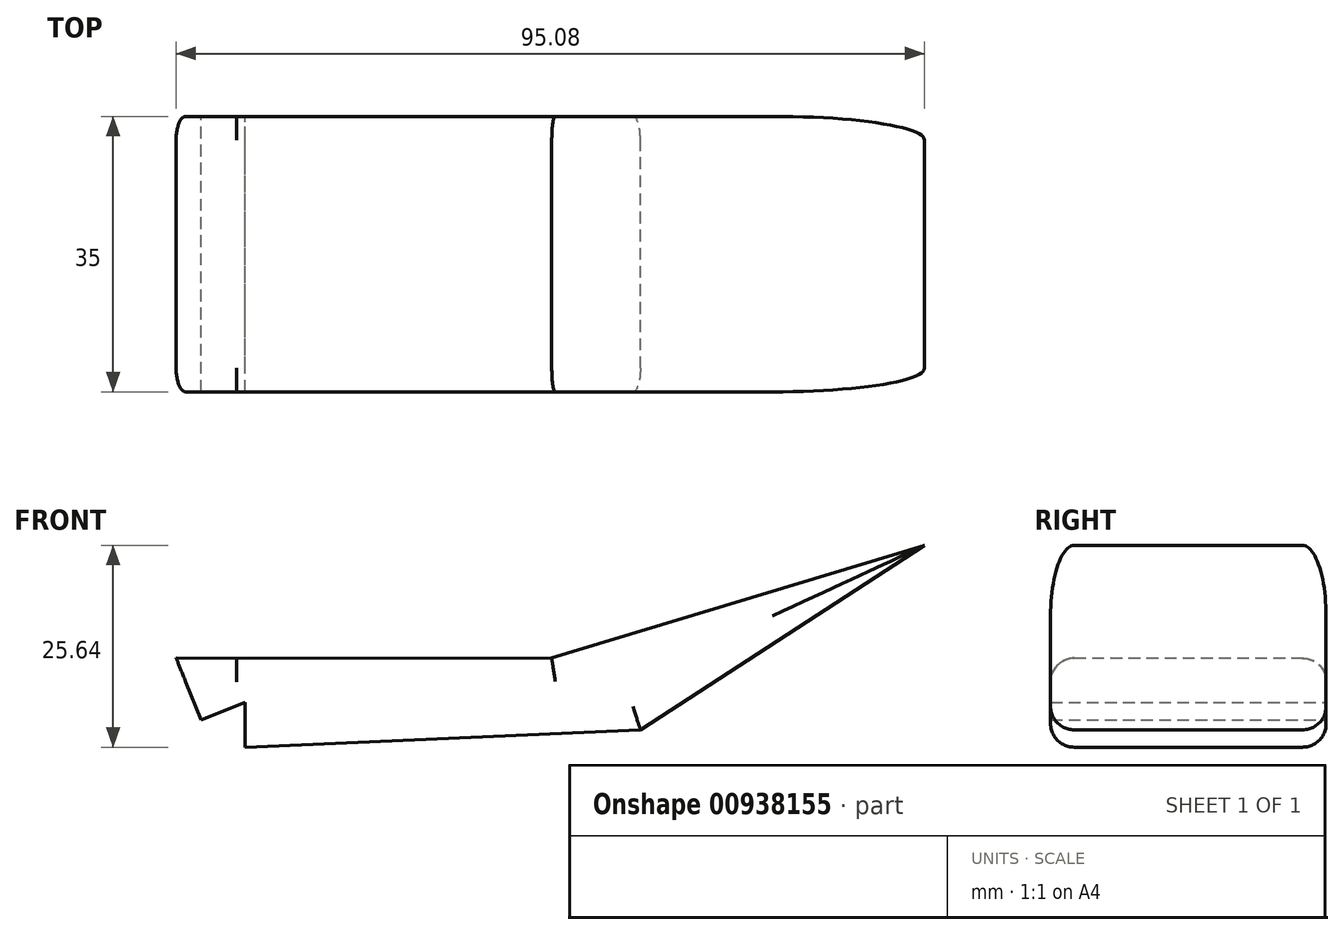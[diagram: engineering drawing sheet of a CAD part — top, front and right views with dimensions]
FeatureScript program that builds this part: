
annotation { "Feature Type Name" : "Feature", "Feature Type Description" : "" }
export const myFeature = defineFeature(function(context is Context, id is Id, definition is map)
    precondition{}
    {
        {
            var Q0;
            Q0=qCreatedBy(makeId("Front.planeOp"),FACE);
            var sketch = newSketch(context, id + "F0", { "sketchPlane" : qUnion([Q0])});
            skLineSegment(sketch, "E0.top", {"start": v(22.17, 17.03) * mm, "end": v(22.25, 17.03) * mm});
            skPoint(sketch, "E1.end.orphan", {"position": v(-65.47, 12.67) * mm});
            skLineSegment(sketch, "E2", {"start": v(-58, 11.13) * mm, "end": v(-57.85, 11.12) * mm});
            skPoint(sketch, "E3", {"position": v(-57.85, 11.12) * mm});
            skPoint(sketch, "E4", {"position": v(133.99, 7.2) * mm});
            skPoint(sketch, "E5.start.orphan", {"position": v(72.17, 17.03) * mm});
            skPoint(sketch, "E6", {"position": v(-58, 11.13) * mm});
            skPoint(sketch, "E7", {"position": v(-51.13, 14.4) * mm});
            skLineSegment(sketch, "E8", {"start": v(-51.33, 8.85) * mm, "end": v(-51.34, 8.7) * mm});
            skPoint(sketch, "E9.orphan", {"position": v(-54.41, 8.7) * mm});
            skLineSegment(sketch, "E10", {"start": v(-25.47, 11.33) * mm, "end": v(-65.47, 11.28) * mm});
            skLineSegment(sketch, "E11", {"start": v(-65.47, 11.28) * mm, "end": v(-73.2, 11.3) * mm});
            skLineSegment(sketch, "E12", {"start": v(-64.43, 5.7) * mm, "end": v(-64.43, 0) * mm});
            skLineSegment(sketch, "E13", {"start": v(-64.43, 5.7) * mm, "end": v(-69.99, 3.44) * mm});
            skLineSegment(sketch, "E14", {"start": v(-69.99, 3.44) * mm, "end": v(-73.2, 11.3) * mm});
            skLineSegment(sketch, "E15", {"start": v(-25.47, 11.33) * mm, "end": v(21.89, 25.64) * mm});
            skLineSegment(sketch, "E16", {"start": v(21.89, 25.64) * mm, "end": v(-14.21, 2.2) * mm});
            skLineSegment(sketch, "E17", {"start": v(-14.21, 2.2) * mm, "end": v(-64.43, 0) * mm});
            skSolve(sketch);
        }
        {
            var Q0;
            Q0 = qSketchRegion(id + "F0", true);
            extrude(context, id + "F1", {"entities" : qUnion([Q0]), "depth" : 35 * mm, "offsetDistance" : 25 * mm});
        }
        {
            var Q0;
            Q0=makeQuery(id+"F1.opExtrude","CAP_EDGE",EDGE,{"disambiguationData":[OSD([sQuery(id+"F0.wireOp",EDGE,"c64adc78-6d33-43d3-98d6-83bfb307d71b"),sQuery(id+"F0.wireOp",EDGE,"cc6a2457-d3de-4c29-8569-52ca4813179c.bottom"),sQuery(id+"F0.wireOp",EDGE,"8b97934e-a699-4df0-9aad-3340579e1050")])],"isStart":false});
            var Q1;
            Q1=makeQuery(id+"F1.opExtrude","CAP_EDGE",EDGE,{"disambiguationData":[OSD([sQuery(id+"F0.wireOp",EDGE,"ekb2hTgJ-wqsG-lHXq-dq90-sHrjzxlNZVmj")])],"isStart":false});
            var Q2;
            Q2=makeQuery(id+"F1.opExtrude","CAP_EDGE",EDGE,{"disambiguationData":[OSD([sQuery(id+"F0.wireOp",EDGE,"ekb2hTgJ-wqsG-lHXq-dq90-sHrjzxlNZVmj")])],"isStart":true});
            var Q3;
            Q3=makeQuery(id+"F1.opExtrude","CAP_EDGE",EDGE,{"disambiguationData":[OSD([sQuery(id+"F0.wireOp",EDGE,"c64adc78-6d33-43d3-98d6-83bfb307d71b"),sQuery(id+"F0.wireOp",EDGE,"cc6a2457-d3de-4c29-8569-52ca4813179c.bottom"),sQuery(id+"F0.wireOp",EDGE,"8b97934e-a699-4df0-9aad-3340579e1050")])],"isStart":true});
            var Q4;
            Q4=makeQuery(id+"F1.opExtrude","CAP_EDGE",EDGE,{"disambiguationData":[OSD([sQuery(id+"F0.wireOp",EDGE,"e85a5ce4-c51d-445c-8a17-c42452e7149c")])],"isStart":true});
            var Q5;
            Q5=makeQuery(id+"F1.opExtrude","CAP_EDGE",EDGE,{"disambiguationData":[OSD([sQuery(id+"F0.wireOp",EDGE,"e85a5ce4-c51d-445c-8a17-c42452e7149c")])],"isStart":false});
            var Q6;
            Q6=makeQuery(id+"F1.opExtrude","CAP_EDGE",EDGE,{"disambiguationData":[OSD([sQuery(id+"F0.wireOp",EDGE,"MHZGYOpM-b0q1-XWYR-XQJK-ZGjIVgK0oyr0")])],"isStart":false});
            var Q7;
            Q7=makeQuery(id+"F1.opExtrude","CAP_EDGE",EDGE,{"disambiguationData":[OSD([sQuery(id+"F0.wireOp",EDGE,"MHZGYOpM-b0q1-XWYR-XQJK-ZGjIVgK0oyr0")])],"isStart":true});
            var Q8;
            Q8=makeQuery(id+"F1.opExtrude","CAP_EDGE",EDGE,{"disambiguationData":[OSD([sQuery(id+"F0.wireOp",EDGE,"E10")])],"isStart":false});
            var Q9;
            Q9=makeQuery(id+"F1.opExtrude","CAP_EDGE",EDGE,{"disambiguationData":[OSD([sQuery(id+"F0.wireOp",EDGE,"E17")])],"isStart":false});
            var Q10;
            Q10=makeQuery(id+"F1.opExtrude","CAP_EDGE",EDGE,{"disambiguationData":[OSD([sQuery(id+"F0.wireOp",EDGE,"E15")])],"isStart":false});
            var Q11;
            Q11=makeQuery(id+"F1.opExtrude","CAP_EDGE",EDGE,{"disambiguationData":[OSD([sQuery(id+"F0.wireOp",EDGE,"E16")])],"isStart":false});
            var Q12;
            Q12=makeQuery(id+"F1.opExtrude","CAP_EDGE",EDGE,{"disambiguationData":[OSD([sQuery(id+"F0.wireOp",EDGE,"E15")])],"isStart":true});
            var Q13;
            Q13=makeQuery(id+"F1.opExtrude","CAP_EDGE",EDGE,{"disambiguationData":[OSD([sQuery(id+"F0.wireOp",EDGE,"E16")])],"isStart":true});
            var Q14;
            Q14=makeQuery(id+"F1.opExtrude","CAP_EDGE",EDGE,{"disambiguationData":[OSD([sQuery(id+"F0.wireOp",EDGE,"E17")])],"isStart":true});
            var Q15;
            Q15=makeQuery(id+"F1.opExtrude","CAP_EDGE",EDGE,{"disambiguationData":[OSD([sQuery(id+"F0.wireOp",EDGE,"E10")])],"isStart":true});
            fillet(context, id + "F2", {"entities" : qUnion([Q0, Q1, Q2, Q3, Q4, Q5, Q6, Q7, Q8, Q9, Q10, Q11, Q12, Q13, Q14, Q15]), "radius" : 3 * mm, "tangentPropagation" : true, "allowEdgeOverflow" : false});
        }
    });
